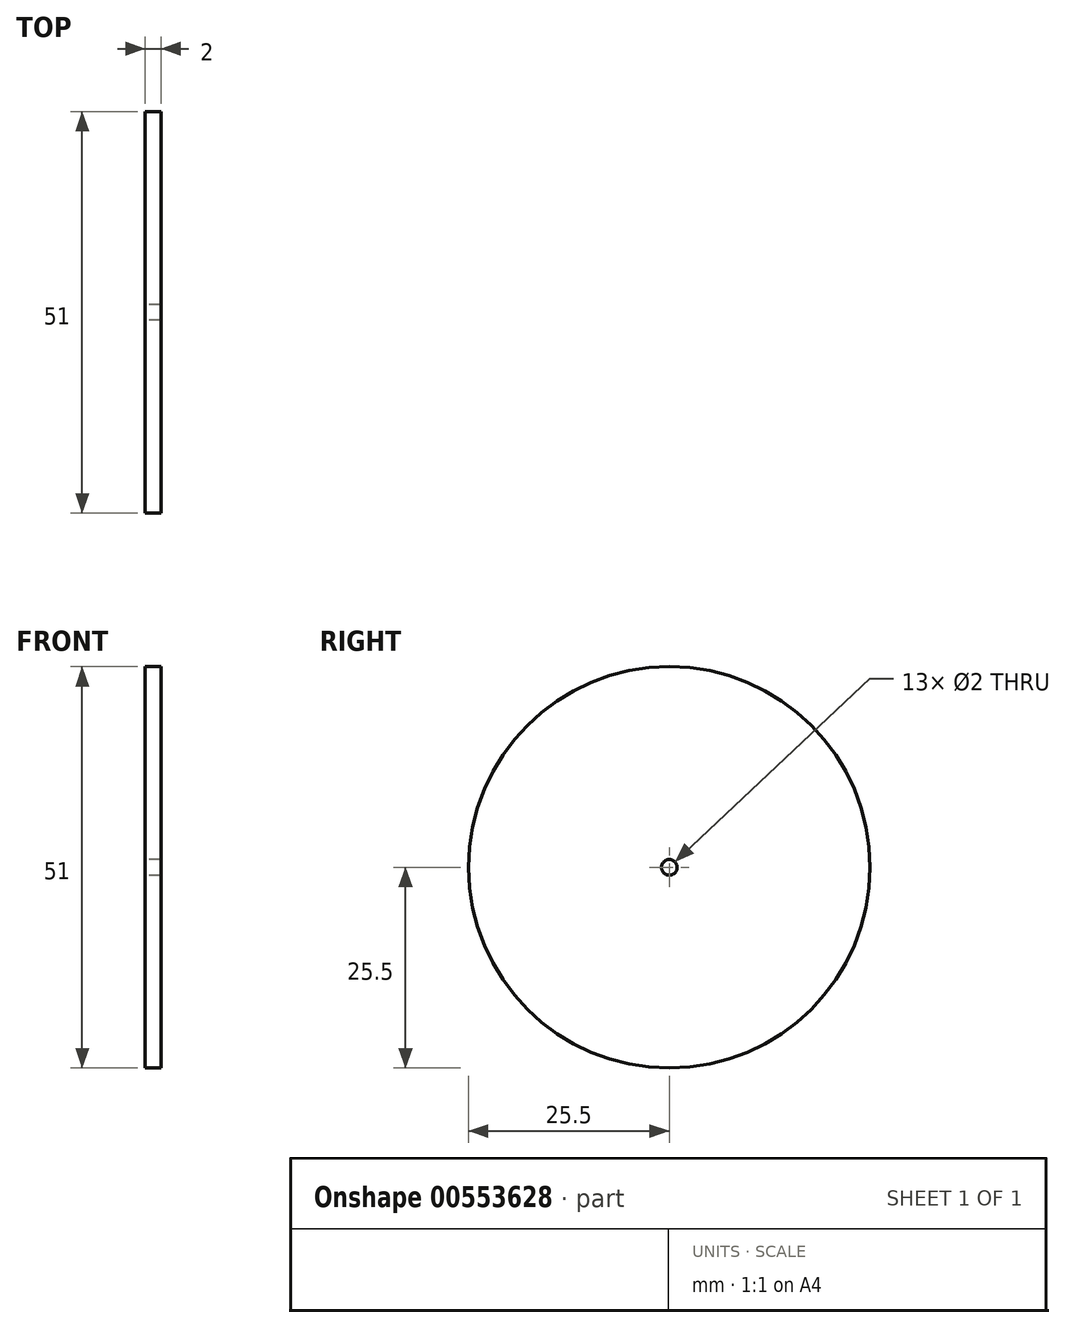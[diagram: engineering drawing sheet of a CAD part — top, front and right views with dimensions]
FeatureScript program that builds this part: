
annotation { "Feature Type Name" : "Feature", "Feature Type Description" : "" }
export const myFeature = defineFeature(function(context is Context, id is Id, definition is map)
    precondition{}
    {
        {
            var Q0;
            Q0=qCreatedBy(makeId("Right.planeOp"),FACE);
            var sketch = newSketch(context, id + "F0", { "sketchPlane" : qUnion([Q0])});
            skCircle(sketch, "E0", {"center": v(0, 0) * mm, "radius": 25.5 * mm});
            skCircle(sketch, "E1", {"center": v(0, 0) * mm, "radius": 1 * mm});
            skSolve(sketch);
        }
        {
            var Q0;
            Q0 = qSketchRegion(id + "F0", true);
            extrude(context, id + "F1", {"entities" : qUnion([Q0]), "depth" : 2 * mm, "offsetDistance" : 25 * mm});
        }
    });
